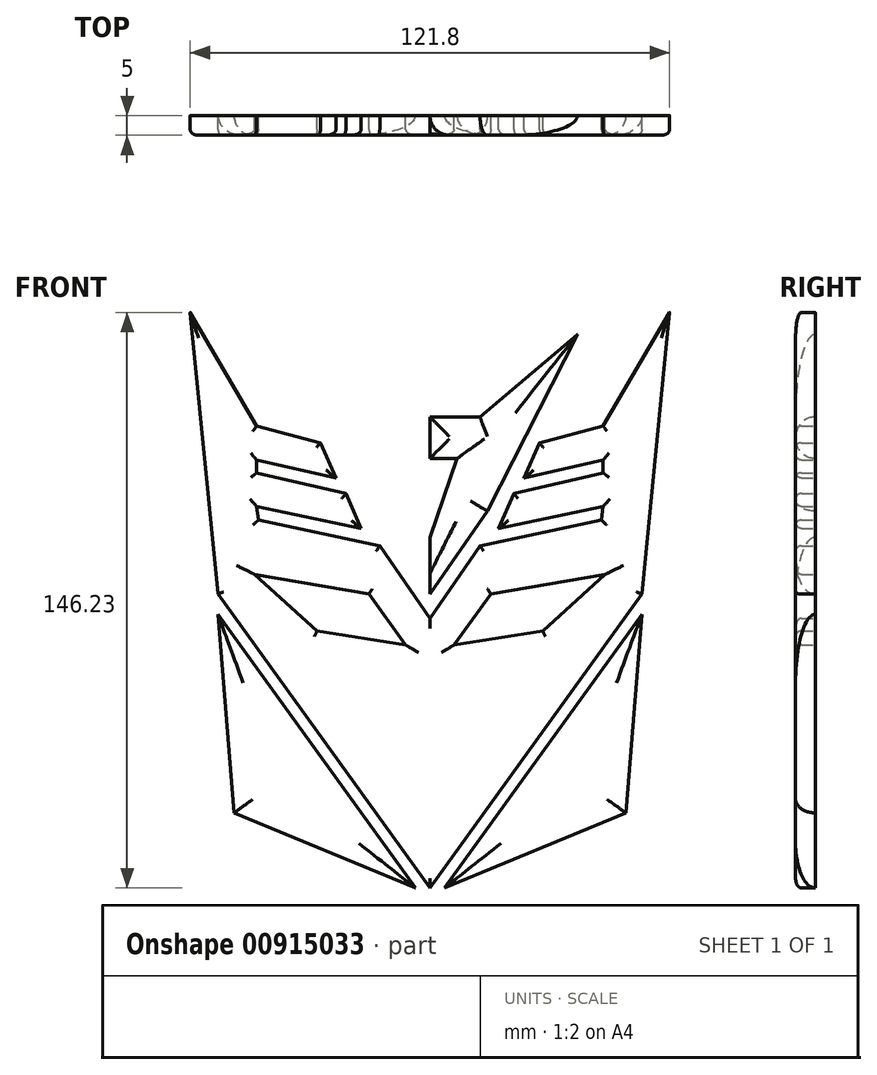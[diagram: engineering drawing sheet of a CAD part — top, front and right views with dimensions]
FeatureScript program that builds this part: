
annotation { "Feature Type Name" : "Feature", "Feature Type Description" : "" }
export const myFeature = defineFeature(function(context is Context, id is Id, definition is map)
    precondition{}
    {
        {
            var Q0;
            Q0=qCreatedBy(makeId("Front.planeOp"),FACE);
            var sketch = newSketch(context, id + "F0", { "sketchPlane" : qUnion([Q0])});
            skLineSegment(sketch, "E0", {"start": v(-12.74, 45) * mm, "end": v(0, 45) * mm});
            skLineSegment(sketch, "E1", {"start": v(0, 45) * mm, "end": v(-12.74, 45) * mm});
            skLineSegment(sketch, "E2", {"start": v(0, 34.44) * mm, "end": v(-6.89, 34.44) * mm});
            skLineSegment(sketch, "E3", {"start": v(0, -74.66) * mm, "end": v(-53.86, 0) * mm});
            skLineSegment(sketch, "E4", {"start": v(-3.7, -74.66) * mm, "end": v(-53.86, -5.13) * mm});
            skLineSegment(sketch, "E5", {"start": v(-53.86, -5.13) * mm, "end": v(-49.75, -55.6) * mm});
            skLineSegment(sketch, "E6", {"start": v(-49.75, -55.6) * mm, "end": v(-3.7, -74.66) * mm});
            skLineSegment(sketch, "E7", {"start": v(-44.03, 42.66) * mm, "end": v(-27.8, 38.42) * mm});
            skLineSegment(sketch, "E8", {"start": v(-27.8, 38.42) * mm, "end": v(-23.89, 29.45) * mm});
            skLineSegment(sketch, "E9", {"start": v(-23.89, 29.45) * mm, "end": v(-44.03, 34.02) * mm});
            skLineSegment(sketch, "E10", {"start": v(-44.03, 34.02) * mm, "end": v(-44.03, 30.8) * mm});
            skLineSegment(sketch, "E11", {"start": v(-44.03, 30.8) * mm, "end": v(-21.34, 25.52) * mm});
            skLineSegment(sketch, "E12", {"start": v(-21.34, 25.52) * mm, "end": v(-17.49, 16.66) * mm});
            skLineSegment(sketch, "E13", {"start": v(-17.49, 16.66) * mm, "end": v(-44.03, 22.3) * mm});
            skLineSegment(sketch, "E14", {"start": v(-44.03, 22.3) * mm, "end": v(-43.58, 18.78) * mm});
            skLineSegment(sketch, "E15", {"start": v(-43.58, 18.78) * mm, "end": v(-12.74, 12.24) * mm});
            skLineSegment(sketch, "E16", {"start": v(-12.74, 12.24) * mm, "end": v(0, -6.16) * mm});
            skLineSegment(sketch, "E17", {"start": v(0, -6.16) * mm, "end": v(-12.74, 12.24) * mm});
            skLineSegment(sketch, "E18", {"start": v(-44.03, 42.66) * mm, "end": v(-60.9, 71.57) * mm});
            skLineSegment(sketch, "E19", {"start": v(-53.86, 0) * mm, "end": v(-60.9, 71.57) * mm});
            skLineSegment(sketch, "E20", {"start": v(-15.48, 0) * mm, "end": v(-6.16, -12.92) * mm});
            skLineSegment(sketch, "E21", {"start": v(-6.16, -12.92) * mm, "end": v(-28.67, -9.38) * mm});
            skLineSegment(sketch, "E22", {"start": v(-28.67, -9.38) * mm, "end": v(-44.51, 4.99) * mm});
            skLineSegment(sketch, "E23", {"start": v(-44.51, 4.99) * mm, "end": v(-28.67, -9.38) * mm});
            skLineSegment(sketch, "E24", {"start": v(-15.48, 0) * mm, "end": v(-44.51, 4.99) * mm});
            skLineSegment(sketch, "E25", {"start": v(0, 0) * mm, "end": v(-14.6, 21.1) * mm});
            skLineSegment(sketch, "E26", {"start": v(-14.6, 21.1) * mm, "end": v(-37.47, 66) * mm});
            skLineSegment(sketch, "E27", {"start": v(-12.74, 45) * mm, "end": v(-37.47, 66) * mm});
            skLineSegment(sketch, "E28", {"start": v(0, 75.82) * mm, "end": v(0, -74.66) * mm});
            skLineSegment(sketch, "E29.MirrorCS", {"start": v(44.03, 34.02) * mm, "end": v(44.03, 30.8) * mm});
            skLineSegment(sketch, "E30.MirrorCS", {"start": v(44.03, 22.3) * mm, "end": v(43.58, 18.78) * mm});
            skLineSegment(sketch, "E31.MirrorCS", {"start": v(27.8, 38.42) * mm, "end": v(23.89, 29.45) * mm});
            skLineSegment(sketch, "E32.MirrorCS", {"start": v(12.74, 45) * mm, "end": v(0, 45) * mm});
            skLineSegment(sketch, "E33.MirrorCS", {"start": v(44.51, 4.99) * mm, "end": v(28.67, -9.38) * mm});
            skLineSegment(sketch, "E34.MirrorCS", {"start": v(0, -6.16) * mm, "end": v(12.74, 12.24) * mm});
            skLineSegment(sketch, "E35.MirrorCS", {"start": v(44.03, 30.8) * mm, "end": v(21.34, 25.52) * mm});
            skLineSegment(sketch, "E36.MirrorCS", {"start": v(3.7, -74.66) * mm, "end": v(53.86, -5.13) * mm});
            skLineSegment(sketch, "E37.MirrorCS", {"start": v(14.6, 21.1) * mm, "end": v(37.47, 66) * mm});
            skLineSegment(sketch, "E38.MirrorCS", {"start": v(23.89, 29.45) * mm, "end": v(44.03, 34.02) * mm});
            skLineSegment(sketch, "E39.MirrorCS", {"start": v(0, 0) * mm, "end": v(14.6, 21.1) * mm});
            skLineSegment(sketch, "E40.MirrorCS", {"start": v(6.16, -12.92) * mm, "end": v(28.67, -9.38) * mm});
            skLineSegment(sketch, "E41.MirrorCS", {"start": v(12.74, 45) * mm, "end": v(37.47, 66) * mm});
            skLineSegment(sketch, "E42.MirrorCS", {"start": v(53.86, -5.13) * mm, "end": v(49.75, -55.6) * mm});
            skLineSegment(sketch, "E43.MirrorCS", {"start": v(44.03, 42.66) * mm, "end": v(27.8, 38.42) * mm});
            skLineSegment(sketch, "E44.MirrorCS", {"start": v(17.49, 16.66) * mm, "end": v(44.03, 22.3) * mm});
            skLineSegment(sketch, "E45.MirrorCS", {"start": v(15.48, 0) * mm, "end": v(44.51, 4.99) * mm});
            skLineSegment(sketch, "E46.MirrorCS", {"start": v(21.34, 25.52) * mm, "end": v(17.49, 16.66) * mm});
            skLineSegment(sketch, "E47.MirrorCS", {"start": v(0, -74.66) * mm, "end": v(53.86, 0) * mm});
            skLineSegment(sketch, "E48.MirrorCS", {"start": v(53.86, 0) * mm, "end": v(60.9, 71.57) * mm});
            skLineSegment(sketch, "E49.MirrorCS", {"start": v(0, 34.44) * mm, "end": v(6.89, 34.44) * mm});
            skLineSegment(sketch, "E50.MirrorCS", {"start": v(12.74, 12.24) * mm, "end": v(0, -6.16) * mm});
            skLineSegment(sketch, "E51.MirrorCS", {"start": v(15.48, 0) * mm, "end": v(6.16, -12.92) * mm});
            skLineSegment(sketch, "E52.MirrorCS", {"start": v(0, 45) * mm, "end": v(12.74, 45) * mm});
            skLineSegment(sketch, "E53.MirrorCS", {"start": v(28.67, -9.38) * mm, "end": v(44.51, 4.99) * mm});
            skLineSegment(sketch, "E54.MirrorCS", {"start": v(43.58, 18.78) * mm, "end": v(12.74, 12.24) * mm});
            skLineSegment(sketch, "E55.MirrorCS", {"start": v(44.03, 42.66) * mm, "end": v(60.9, 71.57) * mm});
            skLineSegment(sketch, "E56", {"start": v(49.75, -55.6) * mm, "end": v(3.7, -74.66) * mm});
            skLineSegment(sketch, "E57", {"start": v(-6.89, 34.44) * mm, "end": v(0, 14.44) * mm});
            skLineSegment(sketch, "E58", {"start": v(0, 14.44) * mm, "end": v(6.89, 34.44) * mm});
            skSolve(sketch);
        }
        {
            var Q0;
            {var subQ0=sQuery(id+"F0.wireOp",EDGE,"E3");Q0=makeQuery(id+"F0.imprint","IMPRINT",FACE,{"disambiguationData":[TD([[makeQuery(id+"F0.imprint","IMPRINT",EDGE,{"derivedFrom":subQ0}),-1.0]])]});}
            var Q1;
            {var subQ2=sQuery(id+"F0.wireOp",EDGE,"E1");Q1=makeQuery(id+"F0.imprint","IMPRINT",FACE,{"disambiguationData":[TD([[makeQuery(id+"F0.imprint","IMPRINT",EDGE,{"derivedFrom":subQ2}),1.0]])]});}
            var Q2;
            Q2=makeQuery(id+"F0.imprint","IMPRINT",FACE,{"disambiguationData":[TD([[makeQuery(id+"F0.imprint","IMPRINT",EDGE,{"derivedFrom":sQuery(id+"F0.wireOp",EDGE,"E37.MirrorCS")}),1.0]])]});
            var Q3;
            Q3=makeQuery(id+"F0.imprint","IMPRINT",FACE,{"disambiguationData":[TD([[makeQuery(id+"F0.imprint","IMPRINT",EDGE,{"derivedFrom":sQuery(id+"F0.wireOp",EDGE,"E29.MirrorCS")}),1.0]])]});
            var Q4;
            Q4=makeQuery(id+"F0.imprint","IMPRINT",FACE,{"disambiguationData":[TD([[makeQuery(id+"F0.imprint","IMPRINT",EDGE,{"derivedFrom":sQuery(id+"F0.wireOp",EDGE,"E36.MirrorCS")}),-1.0]])]});
            var Q5;
            Q5=makeQuery(id+"F0.imprint","IMPRINT",FACE,{"disambiguationData":[TD([[makeQuery(id+"F0.imprint","IMPRINT",EDGE,{"derivedFrom":sQuery(id+"F0.wireOp",EDGE,"E4")}),1.0]])]});
            extrude(context, id + "F1", {"entities" : qUnion([Q0, Q1, Q2, Q3, Q4, Q5]), "depth" : 5 * mm, "offsetDistance" : 25 * mm});
        }
        {
            var Q0;
            Q0=makeQuery(id+"F1.opExtrude","CAP_FACE",FACE,{"disambiguationData":[OSD([sQuery(id+"F0.wireOp",EDGE,"E3"),sQuery(id+"F0.wireOp",EDGE,"E7"),sQuery(id+"F0.wireOp",EDGE,"E8"),sQuery(id+"F0.wireOp",EDGE,"E9"),sQuery(id+"F0.wireOp",EDGE,"E10"),sQuery(id+"F0.wireOp",EDGE,"E11"),sQuery(id+"F0.wireOp",EDGE,"E12"),sQuery(id+"F0.wireOp",EDGE,"E13"),sQuery(id+"F0.wireOp",EDGE,"E14"),sQuery(id+"F0.wireOp",EDGE,"E15"),sQuery(id+"F0.wireOp",EDGE,"E17"),sQuery(id+"F0.wireOp",EDGE,"E18"),sQuery(id+"F0.wireOp",EDGE,"E19"),sQuery(id+"F0.wireOp",EDGE,"E20"),sQuery(id+"F0.wireOp",EDGE,"E21"),sQuery(id+"F0.wireOp",EDGE,"E23"),sQuery(id+"F0.wireOp",EDGE,"E24"),sQuery(id+"F0.wireOp",EDGE,"E29.MirrorCS"),sQuery(id+"F0.wireOp",EDGE,"E30.MirrorCS"),sQuery(id+"F0.wireOp",EDGE,"E31.MirrorCS"),sQuery(id+"F0.wireOp",EDGE,"E35.MirrorCS"),sQuery(id+"F0.wireOp",EDGE,"E38.MirrorCS"),sQuery(id+"F0.wireOp",EDGE,"E40.MirrorCS"),sQuery(id+"F0.wireOp",EDGE,"E43.MirrorCS"),sQuery(id+"F0.wireOp",EDGE,"E44.MirrorCS"),sQuery(id+"F0.wireOp",EDGE,"E45.MirrorCS"),sQuery(id+"F0.wireOp",EDGE,"E46.MirrorCS"),sQuery(id+"F0.wireOp",EDGE,"E47.MirrorCS"),sQuery(id+"F0.wireOp",EDGE,"E48.MirrorCS"),sQuery(id+"F0.wireOp",EDGE,"E50.MirrorCS"),sQuery(id+"F0.wireOp",EDGE,"E51.MirrorCS"),sQuery(id+"F0.wireOp",EDGE,"E53.MirrorCS"),sQuery(id+"F0.wireOp",EDGE,"E54.MirrorCS"),sQuery(id+"F0.wireOp",EDGE,"E55.MirrorCS")])],"isStart":false});
            var Q1;
            Q1=makeQuery(id+"F1.opExtrude","CAP_EDGE",EDGE,{"disambiguationData":[OSD([sQuery(id+"F0.wireOp",EDGE,"E46.MirrorCS")])],"isStart":false});
            fillet(context, id + "F2", {"entities" : qUnion([Q0, Q1]), "radius" : 1.45 * mm, "tangentPropagation" : true, "allowEdgeOverflow" : false});
        }
        {
            var Q0;
            Q0=makeQuery(id+"F1.opExtrude","CAP_FACE",FACE,{"disambiguationData":[OSD([sQuery(id+"F0.wireOp",EDGE,"E1"),sQuery(id+"F0.wireOp",EDGE,"E2"),sQuery(id+"F0.wireOp",EDGE,"E25"),sQuery(id+"F0.wireOp",EDGE,"E26"),sQuery(id+"F0.wireOp",EDGE,"E27"),sQuery(id+"F0.wireOp",EDGE,"E37.MirrorCS"),sQuery(id+"F0.wireOp",EDGE,"E39.MirrorCS"),sQuery(id+"F0.wireOp",EDGE,"E41.MirrorCS"),sQuery(id+"F0.wireOp",EDGE,"E49.MirrorCS"),sQuery(id+"F0.wireOp",EDGE,"E52.MirrorCS"),sQuery(id+"F0.wireOp",EDGE,"E57"),sQuery(id+"F0.wireOp",EDGE,"E58")])],"isStart":false});
            fillet(context, id + "F3", {"entities" : qUnion([Q0]), "radius" : 5 * mm, "tangentPropagation" : true, "allowEdgeOverflow" : false});
        }
        {
            var Q0;
            Q0=makeQuery(id+"F1.opExtrude","CAP_FACE",FACE,{"disambiguationData":[OSD([sQuery(id+"F0.wireOp",EDGE,"E4"),sQuery(id+"F0.wireOp",EDGE,"E5"),sQuery(id+"F0.wireOp",EDGE,"E6")])],"isStart":false});
            var Q1;
            Q1=makeQuery(id+"F1.opExtrude","CAP_FACE",FACE,{"disambiguationData":[OSD([sQuery(id+"F0.wireOp",EDGE,"E36.MirrorCS"),sQuery(id+"F0.wireOp",EDGE,"E42.MirrorCS"),sQuery(id+"F0.wireOp",EDGE,"E56")])],"isStart":false});
            var Q2;
            Q2=makeQuery(id+"F1.opExtrude","CAP_FACE",FACE,{"disambiguationData":[OSD([sQuery(id+"F0.wireOp",EDGE,"E3"),sQuery(id+"F0.wireOp",EDGE,"E7"),sQuery(id+"F0.wireOp",EDGE,"E8"),sQuery(id+"F0.wireOp",EDGE,"E9"),sQuery(id+"F0.wireOp",EDGE,"E10"),sQuery(id+"F0.wireOp",EDGE,"E11"),sQuery(id+"F0.wireOp",EDGE,"E12"),sQuery(id+"F0.wireOp",EDGE,"E13"),sQuery(id+"F0.wireOp",EDGE,"E14"),sQuery(id+"F0.wireOp",EDGE,"E15"),sQuery(id+"F0.wireOp",EDGE,"E17"),sQuery(id+"F0.wireOp",EDGE,"E18"),sQuery(id+"F0.wireOp",EDGE,"E19"),sQuery(id+"F0.wireOp",EDGE,"E20"),sQuery(id+"F0.wireOp",EDGE,"E21"),sQuery(id+"F0.wireOp",EDGE,"E23"),sQuery(id+"F0.wireOp",EDGE,"E24"),sQuery(id+"F0.wireOp",EDGE,"E29.MirrorCS"),sQuery(id+"F0.wireOp",EDGE,"E30.MirrorCS"),sQuery(id+"F0.wireOp",EDGE,"E31.MirrorCS"),sQuery(id+"F0.wireOp",EDGE,"E35.MirrorCS"),sQuery(id+"F0.wireOp",EDGE,"E38.MirrorCS"),sQuery(id+"F0.wireOp",EDGE,"E40.MirrorCS"),sQuery(id+"F0.wireOp",EDGE,"E43.MirrorCS"),sQuery(id+"F0.wireOp",EDGE,"E44.MirrorCS"),sQuery(id+"F0.wireOp",EDGE,"E45.MirrorCS"),sQuery(id+"F0.wireOp",EDGE,"E46.MirrorCS"),sQuery(id+"F0.wireOp",EDGE,"E47.MirrorCS"),sQuery(id+"F0.wireOp",EDGE,"E48.MirrorCS"),sQuery(id+"F0.wireOp",EDGE,"E50.MirrorCS"),sQuery(id+"F0.wireOp",EDGE,"E51.MirrorCS"),sQuery(id+"F0.wireOp",EDGE,"E53.MirrorCS"),sQuery(id+"F0.wireOp",EDGE,"E54.MirrorCS"),sQuery(id+"F0.wireOp",EDGE,"E55.MirrorCS")])],"isStart":false});
            fillet(context, id + "F4", {"entities" : qUnion([Q0, Q1, Q2]), "radius" : 5 * mm, "tangentPropagation" : true, "allowEdgeOverflow" : false});
        }
        {
            var Q0;
            Q0=makeQuery(id+"F1.opExtrude","CAP_FACE",FACE,{"disambiguationData":[OSD([sQuery(id+"F0.wireOp",EDGE,"E3"),sQuery(id+"F0.wireOp",EDGE,"E7"),sQuery(id+"F0.wireOp",EDGE,"E8"),sQuery(id+"F0.wireOp",EDGE,"E9"),sQuery(id+"F0.wireOp",EDGE,"E10"),sQuery(id+"F0.wireOp",EDGE,"E11"),sQuery(id+"F0.wireOp",EDGE,"E12"),sQuery(id+"F0.wireOp",EDGE,"E13"),sQuery(id+"F0.wireOp",EDGE,"E14"),sQuery(id+"F0.wireOp",EDGE,"E15"),sQuery(id+"F0.wireOp",EDGE,"E17"),sQuery(id+"F0.wireOp",EDGE,"E18"),sQuery(id+"F0.wireOp",EDGE,"E19"),sQuery(id+"F0.wireOp",EDGE,"E20"),sQuery(id+"F0.wireOp",EDGE,"E21"),sQuery(id+"F0.wireOp",EDGE,"E23"),sQuery(id+"F0.wireOp",EDGE,"E24"),sQuery(id+"F0.wireOp",EDGE,"E29.MirrorCS"),sQuery(id+"F0.wireOp",EDGE,"E30.MirrorCS"),sQuery(id+"F0.wireOp",EDGE,"E31.MirrorCS"),sQuery(id+"F0.wireOp",EDGE,"E35.MirrorCS"),sQuery(id+"F0.wireOp",EDGE,"E38.MirrorCS"),sQuery(id+"F0.wireOp",EDGE,"E40.MirrorCS"),sQuery(id+"F0.wireOp",EDGE,"E43.MirrorCS"),sQuery(id+"F0.wireOp",EDGE,"E44.MirrorCS"),sQuery(id+"F0.wireOp",EDGE,"E45.MirrorCS"),sQuery(id+"F0.wireOp",EDGE,"E46.MirrorCS"),sQuery(id+"F0.wireOp",EDGE,"E47.MirrorCS"),sQuery(id+"F0.wireOp",EDGE,"E48.MirrorCS"),sQuery(id+"F0.wireOp",EDGE,"E50.MirrorCS"),sQuery(id+"F0.wireOp",EDGE,"E51.MirrorCS"),sQuery(id+"F0.wireOp",EDGE,"E53.MirrorCS"),sQuery(id+"F0.wireOp",EDGE,"E54.MirrorCS"),sQuery(id+"F0.wireOp",EDGE,"E55.MirrorCS")])],"isStart":true});
            var Q1;
            Q1=makeQuery(id+"F1.opExtrude","CAP_EDGE",EDGE,{"disambiguationData":[OSD([sQuery(id+"F0.wireOp",EDGE,"E46.MirrorCS")])],"isStart":true});
            fillet(context, id + "F5", {"entities" : qUnion([Q0, Q1]), "radius" : 0.02 * mm, "tangentPropagation" : true, "allowEdgeOverflow" : false});
        }
    });
